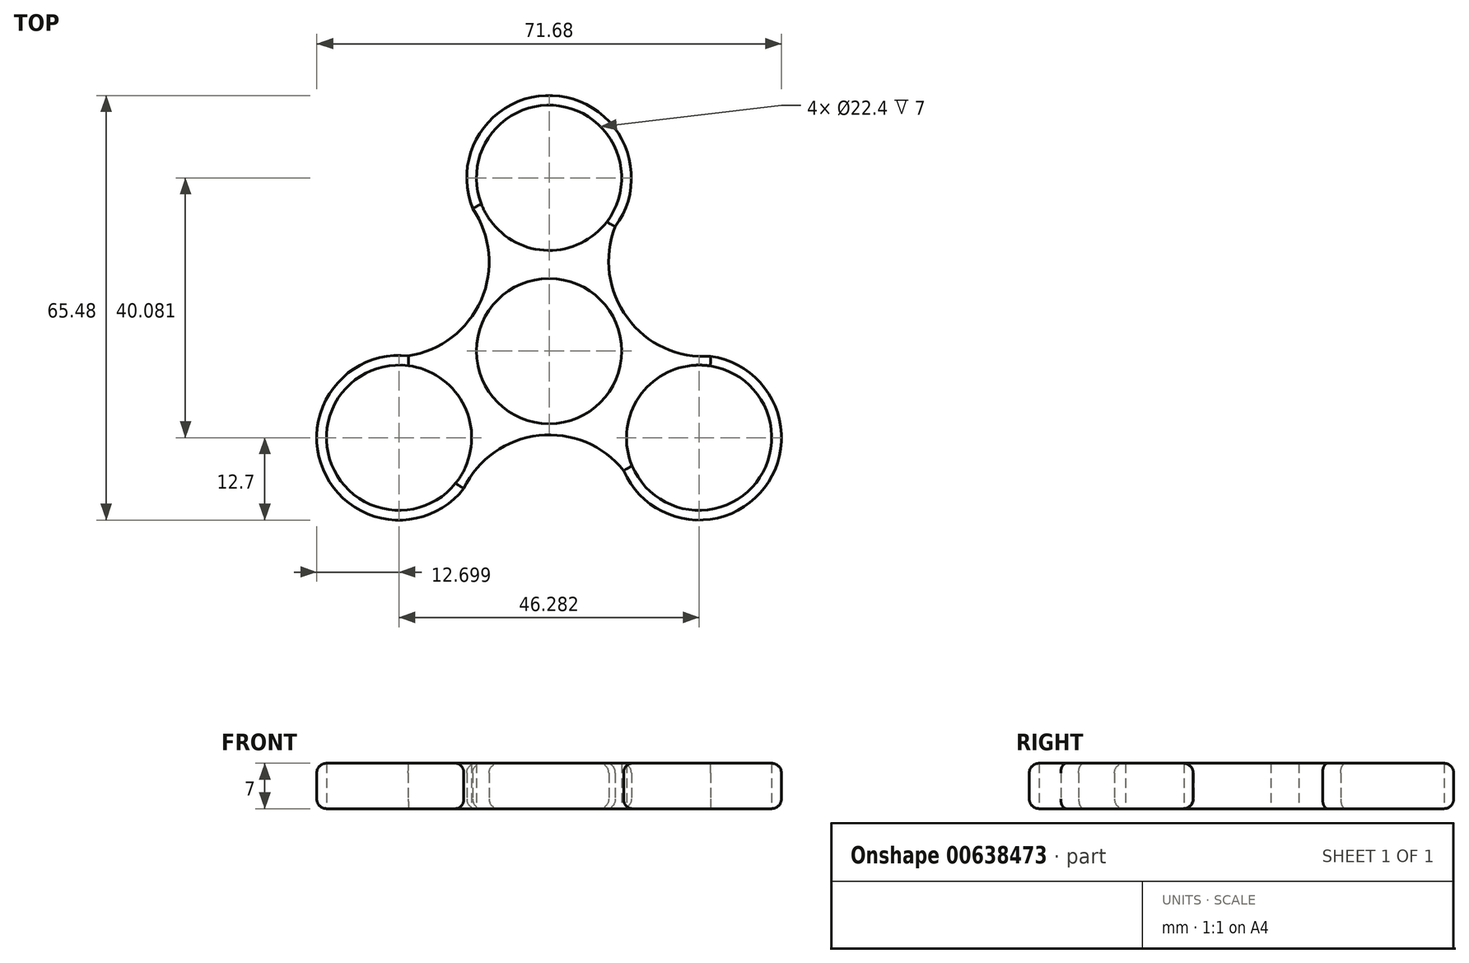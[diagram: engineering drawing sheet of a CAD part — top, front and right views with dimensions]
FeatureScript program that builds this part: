
annotation { "Feature Type Name" : "Feature", "Feature Type Description" : "" }
export const myFeature = defineFeature(function(context is Context, id is Id, definition is map)
    precondition{}
    {
        {
            var Q0;
            Q0=qCreatedBy(makeId("Top.planeOp"),FACE);
            var sketch = newSketch(context, id + "F0", { "sketchPlane" : qUnion([Q0])});
            skCircle(sketch, "E0", {"center": v(0, 0) * mm, "radius": 11.2 * mm});
            skCircle(sketch, "E1", {"center": v(0, 26.72) * mm, "radius": 11.2 * mm});
            skArc(sketch, "E2", {"start": v(10.22, 19.18) * mm, "mid": v(0.15, 39.42) * mm, "end": v(-10.4, 19.42) * mm});
            skCircle(sketch, "E3.1.0", {"center": v(-23.14, -13.36) * mm, "radius": 11.2 * mm});
            skArc(sketch, "E3.1.1", {"start": v(-21.72, -0.74) * mm, "mid": v(-34.21, -19.58) * mm, "end": v(-11.62, -18.71) * mm});
            skCircle(sketch, "E3.2.0", {"center": v(23.14, -13.36) * mm, "radius": 11.2 * mm});
            skArc(sketch, "E3.2.1", {"start": v(11.5, -18.44) * mm, "mid": v(34.06, -19.84) * mm, "end": v(22.01, -0.71) * mm});
            skArc(sketch, "E4", {"start": v(-21.72, -0.74) * mm, "mid": v(-10.48, 7.88) * mm, "end": v(-11.78, 21.99) * mm});
            skArc(sketch, "E5.1.0", {"start": v(11.5, -18.44) * mm, "mid": v(-1.59, -13.01) * mm, "end": v(-13.15, -21.2) * mm});
            skArc(sketch, "E5.2.0", {"start": v(10.22, 19.18) * mm, "mid": v(12.06, 5.13) * mm, "end": v(24.93, -0.79) * mm});
            skSolve(sketch);
        }
        {
            var Q0;
            Q0=makeQuery(id+"F0.imprint","IMPRINT",FACE,{"disambiguationData":[TD([[makeQuery(id+"F0.imprint","IMPRINT",EDGE,{"derivedFrom":sQuery(id+"F0.wireOp",EDGE,"E0")}),-1.0]])]});
            extrude(context, id + "F1", {"entities" : qUnion([Q0]), "depth" : 7 * mm, "offsetDistance" : 25 * mm});
        }
        {
            var Q0;
            Q0=makeQuery(id+"F1.opExtrude","CAP_EDGE",EDGE,{"disambiguationData":[OSD([sQuery(id+"F0.wireOp",EDGE,"E2")])],"isStart":false});
            var Q1;
            Q1=makeQuery(id+"F1.opExtrude","CAP_EDGE",EDGE,{"disambiguationData":[OSD([sQuery(id+"F0.wireOp",EDGE,"E5.2.0")])],"isStart":false});
            var Q2;
            Q2=makeQuery(id+"F1.opExtrude","CAP_EDGE",EDGE,{"disambiguationData":[OSD([sQuery(id+"F0.wireOp",EDGE,"E3.2.1")])],"isStart":false});
            var Q3;
            Q3=makeQuery(id+"F1.opExtrude","CAP_EDGE",EDGE,{"disambiguationData":[OSD([sQuery(id+"F0.wireOp",EDGE,"E5.1.0")])],"isStart":false});
            var Q4;
            Q4=makeQuery(id+"F1.opExtrude","CAP_EDGE",EDGE,{"disambiguationData":[OSD([sQuery(id+"F0.wireOp",EDGE,"E3.1.1")])],"isStart":false});
            var Q5;
            Q5=makeQuery(id+"F1.opExtrude","CAP_EDGE",EDGE,{"disambiguationData":[OSD([sQuery(id+"F0.wireOp",EDGE,"E4")])],"isStart":false});
            fillet(context, id + "F2", {"entities" : qUnion([Q0, Q1, Q2, Q3, Q4, Q5]), "radius" : 1.5 * mm, "tangentPropagation" : true, "allowEdgeOverflow" : false});
        }
        {
            var Q0;
            Q0=makeQuery(id+"F1.opExtrude","CAP_EDGE",EDGE,{"disambiguationData":[OSD([sQuery(id+"F0.wireOp",EDGE,"E3.1.1")])],"isStart":true});
            var Q1;
            Q1=makeQuery(id+"F1.opExtrude","CAP_EDGE",EDGE,{"disambiguationData":[OSD([sQuery(id+"F0.wireOp",EDGE,"E4")])],"isStart":true});
            var Q2;
            Q2=makeQuery(id+"F1.opExtrude","CAP_EDGE",EDGE,{"disambiguationData":[OSD([sQuery(id+"F0.wireOp",EDGE,"E2")])],"isStart":true});
            var Q3;
            Q3=makeQuery(id+"F1.opExtrude","CAP_EDGE",EDGE,{"disambiguationData":[OSD([sQuery(id+"F0.wireOp",EDGE,"E5.2.0")])],"isStart":true});
            var Q4;
            Q4=makeQuery(id+"F1.opExtrude","CAP_EDGE",EDGE,{"disambiguationData":[OSD([sQuery(id+"F0.wireOp",EDGE,"E3.2.1")])],"isStart":true});
            var Q5;
            Q5=makeQuery(id+"F1.opExtrude","CAP_EDGE",EDGE,{"disambiguationData":[OSD([sQuery(id+"F0.wireOp",EDGE,"E5.1.0")])],"isStart":true});
            fillet(context, id + "F3", {"entities" : qUnion([Q0, Q1, Q2, Q3, Q4, Q5]), "radius" : 1.5 * mm, "tangentPropagation" : true, "allowEdgeOverflow" : false});
        }
    });
